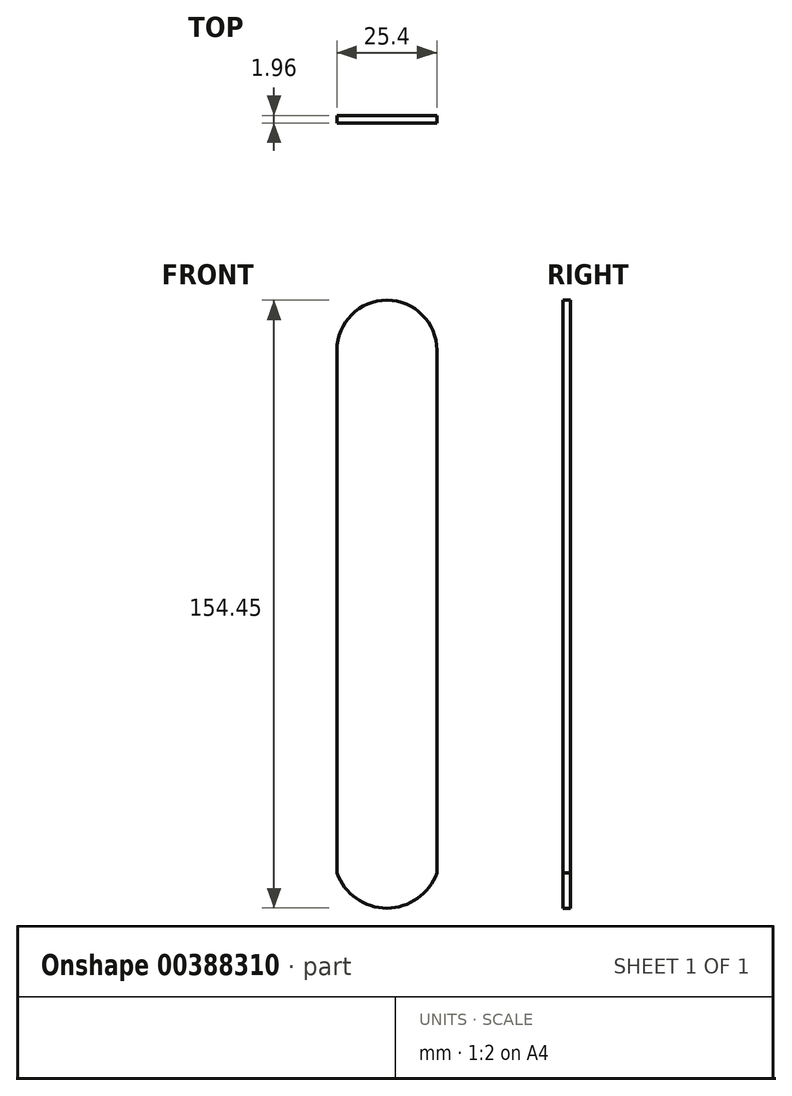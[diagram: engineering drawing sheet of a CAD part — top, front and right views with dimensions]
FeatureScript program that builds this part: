
annotation { "Feature Type Name" : "Feature", "Feature Type Description" : "" }
export const myFeature = defineFeature(function(context is Context, id is Id, definition is map)
    precondition{}
    {
        {
            var Q0;
            Q0=qCreatedBy(makeId("Front.planeOp"),FACE);
            var sketch = newSketch(context, id + "F0", { "sketchPlane" : qUnion([Q0])});
            skLineSegment(sketch, "E0", {"start": v(0, 83) * mm, "end": v(0, -71.84) * mm, "construction": true});
            skLineSegment(sketch, "E1", {"start": v(0, 0) * mm, "end": v(-12.7, 0) * mm, "construction": true});
            skLineSegment(sketch, "E2", {"start": v(0, 0) * mm, "end": v(12.7, 0) * mm, "construction": true});
            skLineSegment(sketch, "E3", {"start": v(-12.7, 0) * mm, "end": v(-12.7, 69.91) * mm});
            skLineSegment(sketch, "E4", {"start": v(12.7, 0) * mm, "end": v(12.7, 69.91) * mm});
            skLineSegment(sketch, "E5", {"start": v(-12.7, 0) * mm, "end": v(-12.7, -62.86) * mm});
            skLineSegment(sketch, "E6", {"start": v(12.7, 0) * mm, "end": v(12.7, -62.86) * mm});
            skArc(sketch, "E7", {"start": v(-12.7, -62.86) * mm, "mid": v(0, -71.84) * mm, "end": v(12.7, -62.86) * mm});
            skArc(sketch, "E8", {"start": v(12.7, 69.91) * mm, "mid": v(0, 82.61) * mm, "end": v(-12.7, 69.91) * mm});
            skSolve(sketch);
        }
        {
            var Q0;
            Q0=qSketchRegion(id+"F0",true);
            var Q1;
            Q1=makeQuery(id+"F0.imprint","IMPRINT",FACE,{"disambiguationData":[TD([[makeQuery(id+"F0.imprint","IMPRINT",EDGE,{"derivedFrom":sQuery(id+"F0.wireOp",EDGE,"E3")}),-1.0]])]});
            extrude(context, id + "F1", {"entities" : qUnion([Q0, Q1]), "depth" : 1.96 * mm});
        }
    });
